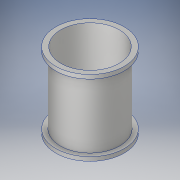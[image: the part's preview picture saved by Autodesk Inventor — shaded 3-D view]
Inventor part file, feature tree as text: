
AUTODESK INVENTOR PART (.ipt)
format: ipt  version: 2018 (Build 220112000, 112)  size: 132,608 bytes
history: native  units: in
note: dims shown in document units (in); Inventor stores cm internally (conversion verified against a paired STEP export)
features: extrude x3, sketch x3
ambient origin geometry x8: Origin, YZ Plane, XZ Plane, XY Plane, X Axis, Y Axis, Z Axis, Center Point
bodies: Solid1 (feature_tree)
feature tree (6):
  extrude  "Extrusion1"  Depth=17.0in
  extrude  "Extrusion2"  Depth=1.0in
  extrude  "Extrusion3"  Depth=16.6875in TaperAngle=0.0deg
  sketch  "Sketch1"  dims[d0=14.5in d1=17.0in]
  sketch  "Sketch2"  dims[d2=1.0in d3=0.0in d4=14.5in]
  sketch  "Sketch3"  dims[d5=14.8in d6=16.6875in d7=0.0in d8=14.5in d9=17.0in d10=1.0in d11=0.0in]
